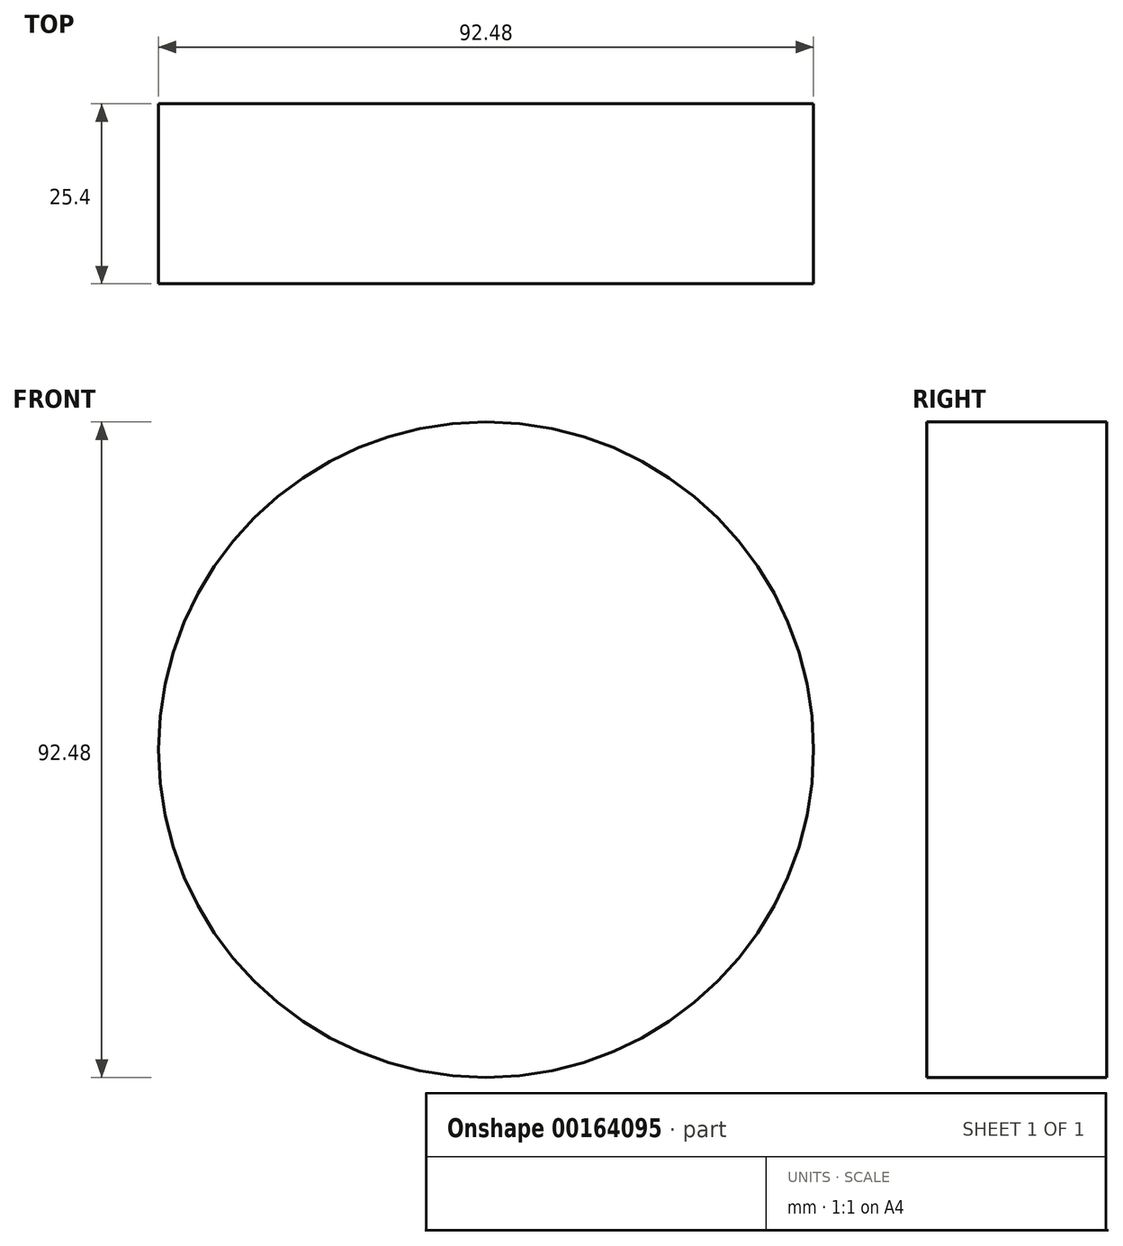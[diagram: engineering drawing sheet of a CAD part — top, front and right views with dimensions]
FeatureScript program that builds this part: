
annotation { "Feature Type Name" : "Feature", "Feature Type Description" : "" }
export const myFeature = defineFeature(function(context is Context, id is Id, definition is map)
    precondition{}
    {
        {
            var Q0;
            Q0=qCreatedBy(makeId("Front.planeOp"),FACE);
            var sketch = newSketch(context, id + "F0", { "sketchPlane" : qUnion([Q0])});
            skCircle(sketch, "E0", {"center": v(0, 0) * mm, "radius": 46.24 * mm});
            skSolve(sketch);
        }
        {
            var Q0;
            Q0=makeQuery(id+"F0.imprint","IMPRINT",FACE,{"disambiguationData":[TD([[makeQuery(id+"F0.imprint","IMPRINT",EDGE,{"derivedFrom":sQuery(id+"F0.wireOp",EDGE,"E0")}),1.0]])]});
            extrude(context, id + "F1", {"entities" : qUnion([Q0]), "depth" : 25.4 * mm});
        }
    });
